# Revit family: Doors_IntSgl_Openable1
name_source: partatom
category: Doors
units: mm (PartAtom-declared; Revit-internal decimal feet)

## family parameters
Always vertical = Yes
Cut with Voids When Loaded = No
Host = Wall
OmniClass Number = 23.30.10.00
OmniClass Title = Doors
Room Calculation Point = No
Shared = No

## types (5) — shared parameters
Analytic Construction = Metal
Construction Type Id = MDOOR
Define Thermal Properties by = Schematic Type
Door Closed = No
Door Open = Yes
Function = Interior
Heat Transfer Coefficient (U) = 3.7021 W/(m²·K)
Thermal Resistance (R) = 0.2701 (m²·K)/W
Thickness = 51 mm
Trim Projection Ext = 25 mm  [stored 0.082021 ft]
Trim Projection Int = 25 mm  [stored 0.082021 ft]
Wall Closure = By host
zero-valued in all types: Solar Heat Gain Coefficient, Visual Light Transmittance

## per-type parameters (varying)
| type | Door Material | Door Width | Frame Material | Height | Trim Width | Width |
| 1830 x 2083mm | Door - Panel | 915 mm | Door - Frame | 2083 mm  [stored 6.83399 ft] | 76 mm  [stored 0.249344 ft] | 1830 mm |
| 1830 x 2134mm | Door - Panel | 915 mm | Door - Frame | 2134 mm  [stored 7.00131 ft] | 76 mm  [stored 0.249344 ft] | 1830 mm |
| 1730 x 2134mm | Door - Panel | 865 mm | Door - Frame | 2134 mm  [stored 7.00131 ft] | 76 mm  [stored 0.249344 ft] | 1730 mm |
| 1730 x 2032mm | Door - Panel | 865 mm | Door - Frame | 2032 mm | 76 mm  [stored 0.249344 ft] | 1730 mm |
| 1200w | Paint - White Lining | 600 mm | Paint - White Lining | 2100 mm | 50 mm | 1200 mm |

note: [stored X ft] marks values corroborated as IEEE doubles in the binary element streams (Revit-internal decimal feet)

## geometry (parser evidence)
native form markers: Sweep x1
no freeform markers — native parametric forms only
